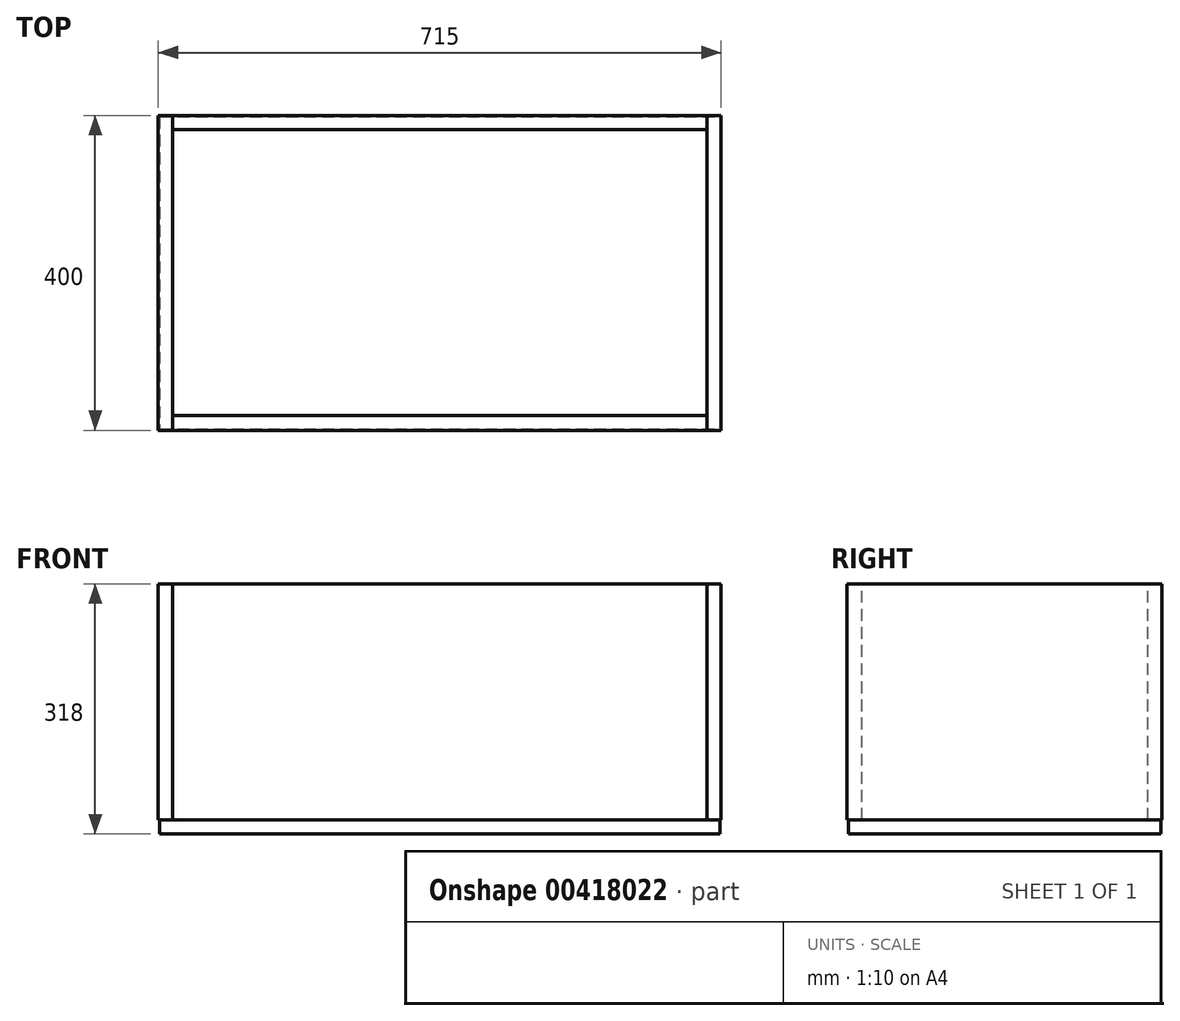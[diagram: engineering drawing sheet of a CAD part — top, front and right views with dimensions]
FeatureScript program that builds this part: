
annotation { "Feature Type Name" : "Feature", "Feature Type Description" : "" }
export const myFeature = defineFeature(function(context is Context, id is Id, definition is map)
    precondition{}
    {
        {
            var Q0;
            Q0=qCreatedBy(makeId("Front.planeOp"),FACE);
            var sketch = newSketch(context, id + "F0", { "sketchPlane" : qUnion([Q0])});
            skLineSegment(sketch, "E0.bottom", {"start": v(-339.5, -150) * mm, "end": v(339.5, -150) * mm});
            skLineSegment(sketch, "E0.top", {"start": v(-339.5, 150) * mm, "end": v(339.5, 150) * mm});
            skLineSegment(sketch, "E0.left", {"start": v(-339.5, -150) * mm, "end": v(-339.5, 150) * mm});
            skLineSegment(sketch, "E0.right", {"start": v(339.5, -150) * mm, "end": v(339.5, 150) * mm});
            skPoint(sketch, "E0.middle", {"position": v(0, 0) * mm});
            skLineSegment(sketch, "E1.bottom", {"start": v(-339.5, -150) * mm, "end": v(-357.5, -150) * mm});
            skLineSegment(sketch, "E1.top", {"start": v(-339.5, 150) * mm, "end": v(-357.5, 150) * mm});
            skLineSegment(sketch, "E1.right", {"start": v(-357.5, -150) * mm, "end": v(-357.5, 150) * mm});
            skLineSegment(sketch, "E2.bottom", {"start": v(339.5, -150) * mm, "end": v(357.5, -150) * mm});
            skLineSegment(sketch, "E2.top", {"start": v(339.5, 150) * mm, "end": v(357.5, 150) * mm});
            skLineSegment(sketch, "E2.right", {"start": v(357.5, -150) * mm, "end": v(357.5, 150) * mm});
            skLineSegment(sketch, "E3", {"start": v(0, 0) * mm, "end": v(0, -312.9) * mm, "construction": true});
            skLineSegment(sketch, "E4.bottom", {"start": v(356, -168) * mm, "end": v(-356, -168) * mm});
            skLineSegment(sketch, "E4.top", {"start": v(356, -150) * mm, "end": v(-356, -150) * mm});
            skLineSegment(sketch, "E4.left", {"start": v(356, -168) * mm, "end": v(356, -150) * mm});
            skLineSegment(sketch, "E4.right", {"start": v(-356, -168) * mm, "end": v(-356, -150) * mm});
            skPoint(sketch, "E4.middle", {"position": v(0, -159) * mm});
            skSolve(sketch);
        }
        {
            var Q0;
            {var subQ1=sQuery(id+"F0.wireOp",EDGE,"E1.bottom");Q0=makeQuery(id+"F0.imprint","IMPRINT",FACE,{"disambiguationData":[TD([[makeQuery(id+"F0.imprint","IMPRINT",EDGE,{"derivedFrom":subQ1}),-1.0]])]});}
            var Q1;
            {var subQ1=sQuery(id+"F0.wireOp",EDGE,"E2.bottom");Q1=makeQuery(id+"F0.imprint","IMPRINT",FACE,{"disambiguationData":[TD([[makeQuery(id+"F0.imprint","IMPRINT",EDGE,{"derivedFrom":subQ1}),1.0]])]});}
            extrude(context, id + "F1", {"entities" : qUnion([Q0, Q1]), "depth" : 400 * mm});
        }
        {
            var Q0;
            Q0=makeQuery(id+"F0.imprint","IMPRINT",FACE,{"disambiguationData":[TD([[makeQuery(id+"F0.imprint","IMPRINT",EDGE,{"derivedFrom":sQuery(id+"F0.wireOp",EDGE,"E0.top")}),-1.0]])]});
            extrude(context, id + "F2", {"entities" : qUnion([Q0]), "depth" : 18 * mm});
        }
        {
            var Q0;
            Q0=makeQuery(id+"F0.imprint","IMPRINT",FACE,{"disambiguationData":[TD([[makeQuery(id+"F0.imprint","IMPRINT",EDGE,{"derivedFrom":sQuery(id+"F0.wireOp",EDGE,"E0.top")}),-1.0]])]});
            cPlane(context, id + "F3", {"entities" : qUnion([Q0]), "cplaneType" : CPlaneType.OFFSET, "offset" : 400 * mm, "width" : 150 * mm, "height" : 150 * mm});
        }
        {
            var Q0;
            Q0=qCreatedBy(id+"F3.planeOp",FACE);
            var sketch = newSketch(context, id + "F4", { "sketchPlane" : qUnion([Q0])});
            skLineSegment(sketch, "E5.bottom", {"start": v(-339.5, -150) * mm, "end": v(339.5, -150) * mm});
            skLineSegment(sketch, "E5.top", {"start": v(-339.5, 150) * mm, "end": v(339.5, 150) * mm});
            skLineSegment(sketch, "E5.left", {"start": v(-339.5, -150) * mm, "end": v(-339.5, 150) * mm});
            skLineSegment(sketch, "E5.right", {"start": v(339.5, -150) * mm, "end": v(339.5, 150) * mm});
            skPoint(sketch, "E5.middle", {"position": v(0, 0) * mm});
            skLineSegment(sketch, "E6.bottom", {"start": v(-339.5, -150) * mm, "end": v(-357.5, -150) * mm});
            skLineSegment(sketch, "E6.top", {"start": v(-339.5, 150) * mm, "end": v(-357.5, 150) * mm});
            skLineSegment(sketch, "E6.right", {"start": v(-357.5, -150) * mm, "end": v(-357.5, 150) * mm});
            skLineSegment(sketch, "E7.bottom", {"start": v(339.5, -150) * mm, "end": v(357.5, -150) * mm});
            skLineSegment(sketch, "E7.top", {"start": v(339.5, 150) * mm, "end": v(357.5, 150) * mm});
            skLineSegment(sketch, "E7.right", {"start": v(357.5, -150) * mm, "end": v(357.5, 150) * mm});
            skLineSegment(sketch, "E8", {"start": v(0, 18.77) * mm, "end": v(0, 0) * mm, "construction": true});
            skLineSegment(sketch, "E9.bottom", {"start": v(356, -168) * mm, "end": v(-356, -168) * mm});
            skLineSegment(sketch, "E9.top", {"start": v(356, -150) * mm, "end": v(-356, -150) * mm});
            skLineSegment(sketch, "E9.left", {"start": v(356, -168) * mm, "end": v(356, -150) * mm});
            skLineSegment(sketch, "E9.right", {"start": v(-356, -168) * mm, "end": v(-356, -150) * mm});
            skPoint(sketch, "E9.middle", {"position": v(0, -159) * mm});
            skSolve(sketch);
        }
        {
            var Q0;
            Q0=makeQuery(id+"F4.imprint","IMPRINT",FACE,{"disambiguationData":[TD([[makeQuery(id+"F4.imprint","IMPRINT",EDGE,{"derivedFrom":sQuery(id+"F4.wireOp",EDGE,"E5.top")}),-1.0]])]});
            extrude(context, id + "F5", {"entities" : qUnion([Q0]), "oppositeDirection" : true, "depth" : 19 * mm});
        }
        {
            var Q0;
            Q0=makeQuery(id+"F5.opExtrude","CAP_FACE",FACE,{"disambiguationData":[OSD([sQuery(id+"F4.wireOp",EDGE,"E5.top"),sQuery(id+"F4.wireOp",EDGE,"E5.left"),sQuery(id+"F4.wireOp",EDGE,"E5.right"),sQuery(id+"F4.wireOp",EDGE,"E9.top")])],"isStart":true});
            cPlane(context, id + "F6", {"entities" : qUnion([Q0]), "cplaneType" : CPlaneType.OFFSET, "offset" : 1.5 * mm, "oppositeDirection" : true, "width" : 150 * mm, "height" : 150 * mm});
        }
        {
            var Q0;
            Q0=qCreatedBy(id+"F6.planeOp",FACE);
            var sketch = newSketch(context, id + "F7", { "sketchPlane" : qUnion([Q0])});
            skLineSegment(sketch, "E10.bottom", {"start": v(-339.5, -150) * mm, "end": v(339.5, -150) * mm});
            skLineSegment(sketch, "E10.top", {"start": v(-339.5, 150) * mm, "end": v(339.5, 150) * mm});
            skLineSegment(sketch, "E10.left", {"start": v(-339.5, -150) * mm, "end": v(-339.5, 150) * mm});
            skLineSegment(sketch, "E10.right", {"start": v(339.5, -150) * mm, "end": v(339.5, 150) * mm});
            skPoint(sketch, "E10.middle", {"position": v(0, 0) * mm});
            skLineSegment(sketch, "E11.bottom", {"start": v(-339.5, -150) * mm, "end": v(-357.5, -150) * mm});
            skLineSegment(sketch, "E11.top", {"start": v(-339.5, 150) * mm, "end": v(-357.5, 150) * mm});
            skLineSegment(sketch, "E11.right", {"start": v(-357.5, -150) * mm, "end": v(-357.5, 150) * mm});
            skLineSegment(sketch, "E12.bottom", {"start": v(339.5, -150) * mm, "end": v(357.5, -150) * mm});
            skLineSegment(sketch, "E12.top", {"start": v(339.5, 150) * mm, "end": v(357.5, 150) * mm});
            skLineSegment(sketch, "E12.right", {"start": v(357.5, -150) * mm, "end": v(357.5, 150) * mm});
            skLineSegment(sketch, "E13", {"start": v(0, 0) * mm, "end": v(0, -81.43) * mm, "construction": true});
            skLineSegment(sketch, "E14.bottom", {"start": v(356, -168) * mm, "end": v(-356, -168) * mm});
            skLineSegment(sketch, "E14.top", {"start": v(356, -150) * mm, "end": v(-356, -150) * mm});
            skLineSegment(sketch, "E14.left", {"start": v(356, -168) * mm, "end": v(356, -150) * mm});
            skLineSegment(sketch, "E14.right", {"start": v(-356, -168) * mm, "end": v(-356, -150) * mm});
            skPoint(sketch, "E14.middle", {"position": v(0, -159) * mm});
            skSolve(sketch);
        }
        {
            var Q0;
            Q0=makeQuery(id+"F7.imprint","IMPRINT",FACE,{"disambiguationData":[TD([[makeQuery(id+"F7.imprint","IMPRINT",EDGE,{"derivedFrom":sQuery(id+"F7.wireOp",EDGE,"E14.bottom")}),-1.0]])]});
            extrude(context, id + "F8", {"entities" : qUnion([Q0]), "oppositeDirection" : true, "depth" : 397 * mm});
        }
    });
